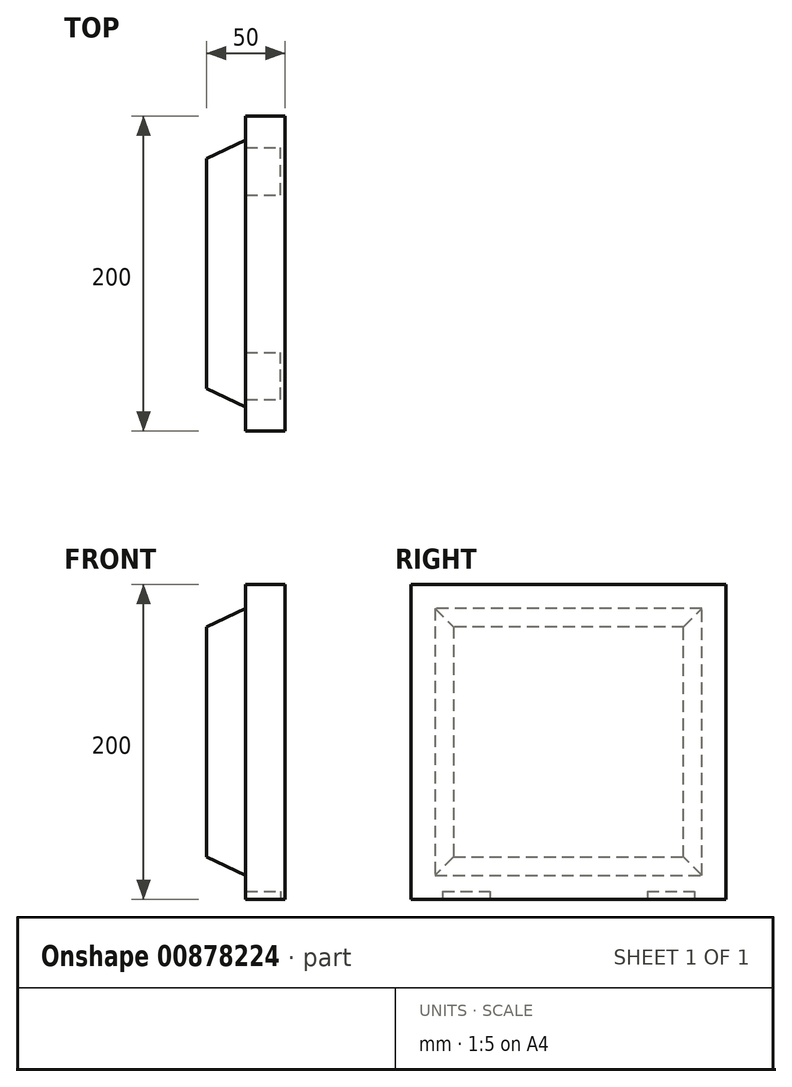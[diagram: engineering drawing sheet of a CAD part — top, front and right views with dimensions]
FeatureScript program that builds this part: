
annotation { "Feature Type Name" : "Feature", "Feature Type Description" : "" }
export const myFeature = defineFeature(function(context is Context, id is Id, definition is map)
    precondition{}
    {
        {
            var Q0;
            Q0=qCreatedBy(makeId("Right.planeOp"),FACE);
            var sketch = newSketch(context, id + "F0", { "sketchPlane" : qUnion([Q0])});
            skLineSegment(sketch, "E0.bottom", {"start": v(0, 0) * mm, "end": v(200, 0) * mm});
            skLineSegment(sketch, "E0.top", {"start": v(0, 200) * mm, "end": v(200, 200) * mm});
            skLineSegment(sketch, "E0.left", {"start": v(0, 0) * mm, "end": v(0, 200) * mm});
            skLineSegment(sketch, "E0.right", {"start": v(200, 0) * mm, "end": v(200, 200) * mm});
            skSolve(sketch);
        }
        {
            var Q0;
            Q0 = qSketchRegion(id + "F0", true);
            extrude(context, id + "F1", {"entities" : qUnion([Q0]), "depth" : 25 * mm, "offsetDistance" : 25 * mm});
        }
        {
            var Q0;
            Q0=makeQuery(id+"F1.opExtrude","CAP_FACE",FACE,{"disambiguationData":[OSD([sQuery(id+"F0.wireOp",EDGE,"E0.bottom"),sQuery(id+"F0.wireOp",EDGE,"E0.top"),sQuery(id+"F0.wireOp",EDGE,"E0.left"),sQuery(id+"F0.wireOp",EDGE,"E0.right")])],"isStart":true});
            var sketch = newSketch(context, id + "F2", { "sketchPlane" : qUnion([Q0])});
            skLineSegment(sketch, "E1.bottom", {"start": v(-184.75, 15.25) * mm, "end": v(-15.25, 15.25) * mm});
            skLineSegment(sketch, "E1.top", {"start": v(-184.75, 184.75) * mm, "end": v(-15.25, 184.75) * mm});
            skLineSegment(sketch, "E1.left", {"start": v(-184.75, 15.25) * mm, "end": v(-184.75, 184.75) * mm});
            skLineSegment(sketch, "E1.right", {"start": v(-15.25, 15.25) * mm, "end": v(-15.25, 184.75) * mm});
            skSolve(sketch);
        }
        {
            var Q0;
            Q0 = qSketchRegion(id + "F2", true);
            extrude(context, id + "F3", {"entities" : qUnion([Q0]), "operationType" : NewBodyOperationType.ADD, "depth" : 25 * mm, "offsetDistance" : 25 * mm, "hasDraft" : true, "draftAngle" : 25 * degree, "draftPullDirection" : true});
        }
        {
            var Q0;
            Q0=makeQuery(id+"F1.opExtrude","SWEPT_FACE",FACE,{"disambiguationData":[OSD([sQuery(id+"F0.wireOp",EDGE,"E0.bottom")])]});
            var sketch = newSketch(context, id + "F4", { "sketchPlane" : qUnion([Q0])});
            skLineSegment(sketch, "E2.bottom", {"start": v(0, -180) * mm, "end": v(22, -180) * mm});
            skLineSegment(sketch, "E2.top", {"start": v(0, -150) * mm, "end": v(22, -150) * mm});
            skLineSegment(sketch, "E2.left", {"start": v(0, -180) * mm, "end": v(0, -150) * mm});
            skLineSegment(sketch, "E3.bottom", {"start": v(0, -20) * mm, "end": v(22, -20) * mm});
            skLineSegment(sketch, "E3.top", {"start": v(0, -50) * mm, "end": v(22, -50) * mm});
            skLineSegment(sketch, "E3.left", {"start": v(0, -20) * mm, "end": v(0, -50) * mm});
            skLineSegment(sketch, "E4", {"start": v(22, -20) * mm, "end": v(22, -50) * mm});
            skLineSegment(sketch, "E5", {"start": v(22, -150) * mm, "end": v(22, -180) * mm});
            skSolve(sketch);
        }
        {
            var Q0;
            Q0=makeQuery(id+"F4.imprint","IMPRINT",FACE,{"disambiguationData":[TD([[makeQuery(id+"F4.imprint","IMPRINT",EDGE,{"derivedFrom":sQuery(id+"F4.wireOp",EDGE,"E2.bottom")}),1.0]])]});
            var Q1;
            Q1=makeQuery(id+"F4.imprint","IMPRINT",FACE,{"disambiguationData":[TD([[makeQuery(id+"F4.imprint","IMPRINT",EDGE,{"derivedFrom":sQuery(id+"F4.wireOp",EDGE,"E3.bottom")}),-1.0]])]});
            extrude(context, id + "F5", {"entities" : qUnion([Q0, Q1]), "operationType" : NewBodyOperationType.REMOVE, "oppositeDirection" : true, "depth" : 5 * mm, "offsetDistance" : 25 * mm});
        }
    });
